# Revit family: KR1165551_Grifería Lavamanos Monocontrol Koral media Niquel
name_source: partatom
category: Generic Models
units: mm (PartAtom-declared; Revit-internal decimal feet)

## family parameters
Always vertical = Yes
Can host rebar = No
Cut with Voids When Loaded = No
Part Type = Normal
Room Calculation Point = No
Round Connector Dimension = Use Diameter
Shared = No
Work Plane-Based = No

## types (1)
- KR1165551_Grifería Lavamanos Monocontrol Koral media Niquel
    Acabado = Corona_Niquel
    Capacidad de flujo estimada real a 60 psi = 5,7 L/min
    Con Tecnología Ecostream = ahorro de agua, consumo máximo de 5,7 litros por minuto
    Con recubrimiento en PVD (deposición de vapor) = Con targets de zirconio que garantizan una gran resistencia a la corrosion
    Creado por = IDD
    Description = La línea de griferías Koral son la mejor opción para tu lavamanos, gracias a su tecnología EcoStream te garantizará ahorro de agua en cada uso y te permitirá mezclar el agua fría y caliente con una sola manija. ¡Cómprala ahora!
    Dimensiones generales del producto = (H x W x L): 330 x 155 x 75 mm
(H x W x L): 13 x 6,10 x 2,95 pulg
    Fecha de creación = 5/10/2020
    Fácil limpieza = Diseño que evita la acumulación de impurezas
    Material = Corona_Metal
    Peso neto = 760 g - 1,67 lb
    Presión de trabajo máximo recomendado = 125 psi (860 Kpa)
    Presión de trabajo mínimo recomendado = 20 psi (140 Kpa)
    Recubrimientos = No tóxicos
    Resistencia de la manija al torque = 5,20 N.m.
    Resistente = Corrosión, pelado y decoloración por agua
    Temperatura máxima de trabajo = 66˚C / 150,8˚F
    Temperatura mínima de trabajo = 5˚C / 41˚F
    URL = https://corona.co
    Uso = Doméstico
    Vida útil del cartucho o unidad de cierre = 500.000 ciclos

## geometry (parser evidence)
native form markers: Sweep x2
no freeform markers — native parametric forms only
